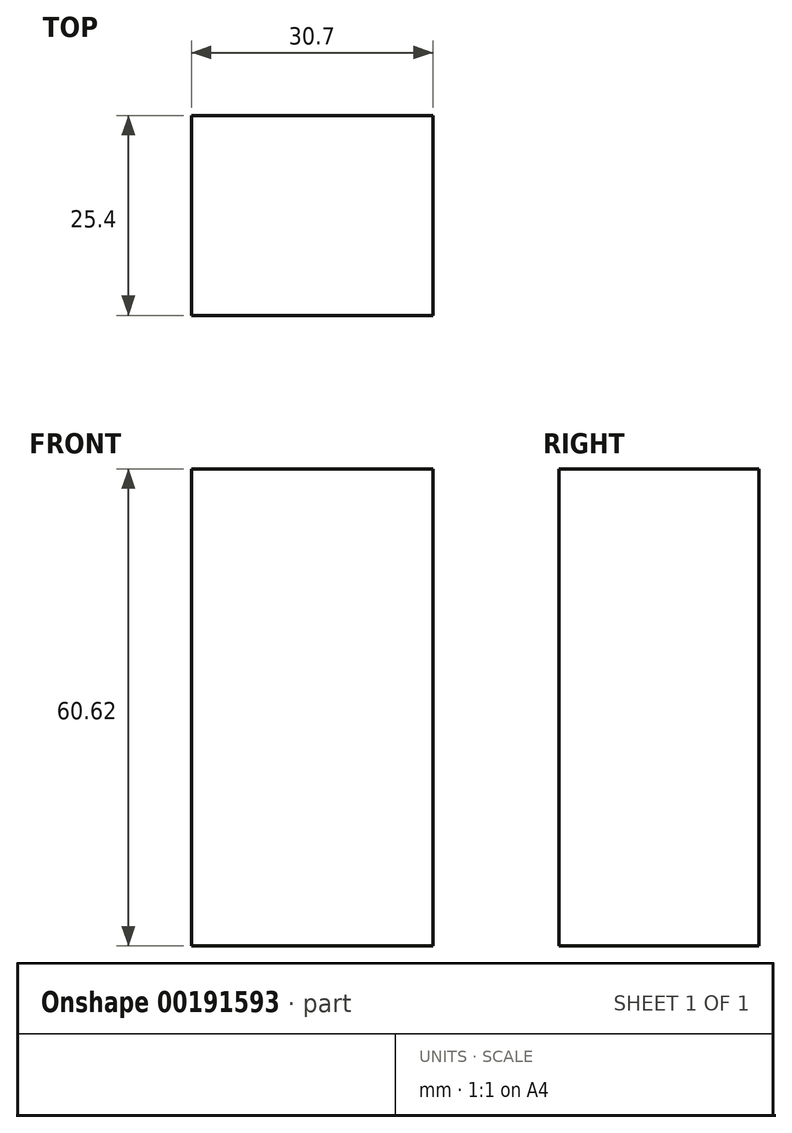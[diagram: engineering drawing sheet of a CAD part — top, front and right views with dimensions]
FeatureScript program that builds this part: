
annotation { "Feature Type Name" : "Feature", "Feature Type Description" : "" }
export const myFeature = defineFeature(function(context is Context, id is Id, definition is map)
    precondition{}
    {
        {
            var Q0;
            Q0=qCreatedBy(makeId("Front.planeOp"),FACE);
            var sketch = newSketch(context, id + "F0", { "sketchPlane" : qUnion([Q0])});
            skLineSegment(sketch, "E0.bottom", {"start": v(15.35, 30.31) * mm, "end": v(-15.35, 30.31) * mm});
            skLineSegment(sketch, "E0.top", {"start": v(15.35, -30.31) * mm, "end": v(-15.35, -30.31) * mm});
            skLineSegment(sketch, "E0.left", {"start": v(15.35, 30.31) * mm, "end": v(15.35, -30.31) * mm});
            skLineSegment(sketch, "E0.right", {"start": v(-15.35, 30.31) * mm, "end": v(-15.35, -30.31) * mm});
            skPoint(sketch, "E0.middle", {"position": v(0, 0) * mm});
            skSolve(sketch);
        }
        {
            var Q0;
            Q0 = qSketchRegion(id + "FFBgE0I4olTfEIv_0", true);
            var Q1;
            Q1 = qSketchRegion(id + "F0", true);
            extrude(context, id + "F1", {"entities" : qUnion([Q0, Q1]), "depth" : 25.4 * mm});
        }
    });
